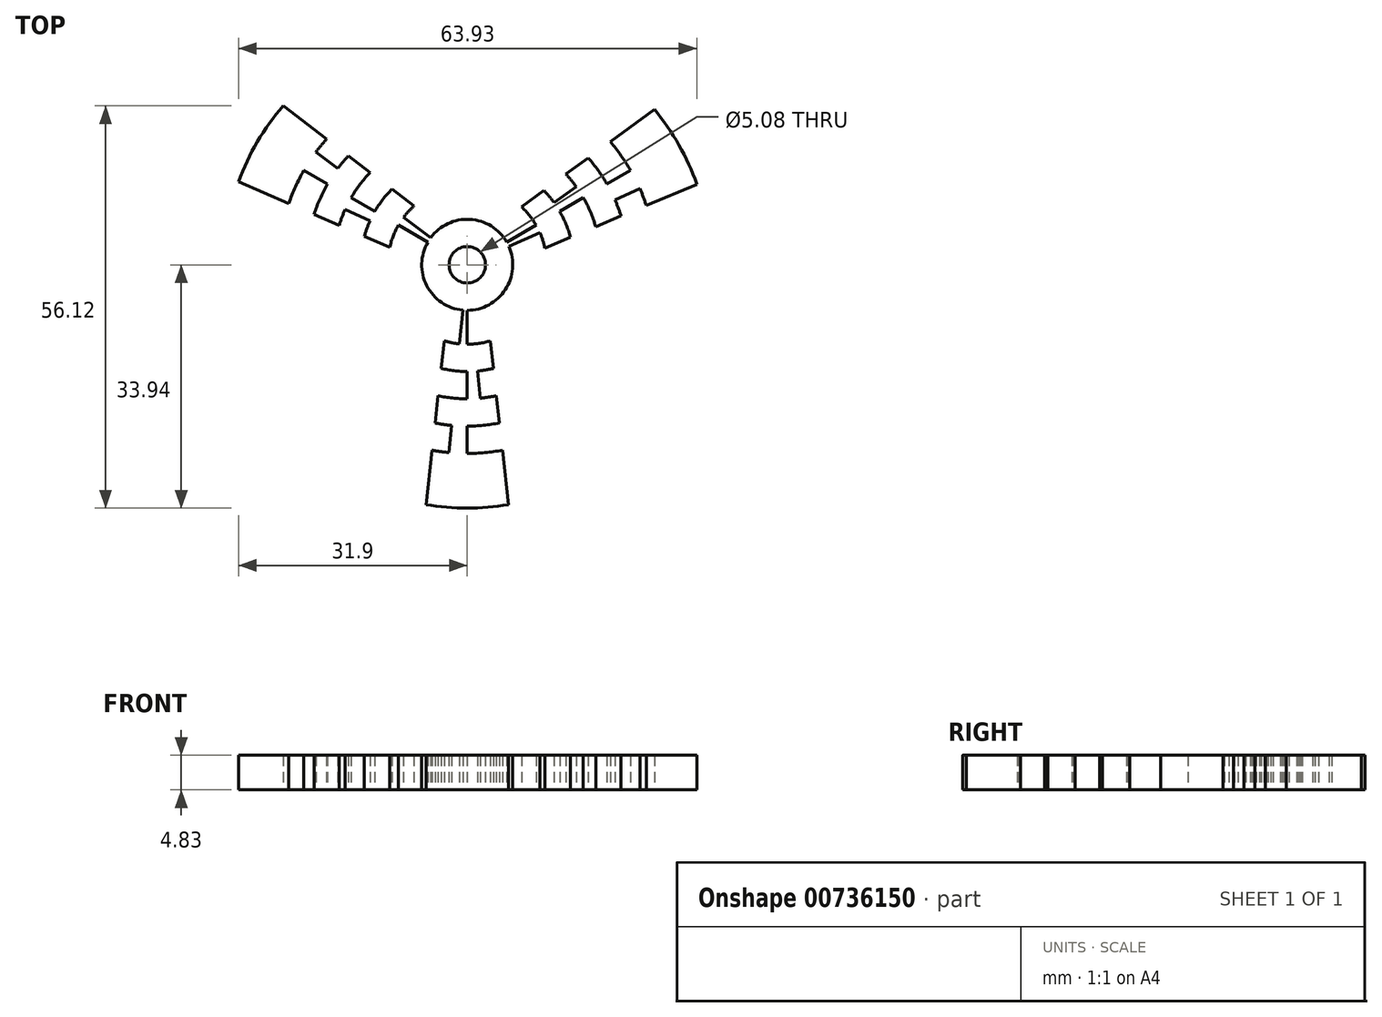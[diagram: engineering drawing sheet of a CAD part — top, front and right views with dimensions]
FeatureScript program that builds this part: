
annotation { "Feature Type Name" : "Feature", "Feature Type Description" : "" }
export const myFeature = defineFeature(function(context is Context, id is Id, definition is map)
    precondition{}
    {
        {
            var Q0;
            Q0=qCreatedBy(makeId("Top.planeOp"),FACE);
            var sketch = newSketch(context, id + "F0", { "sketchPlane" : qUnion([Q0])});
            skCircle(sketch, "E0", {"center": v(0, 0) * mm, "radius": 6.35 * mm});
            skCircle(sketch, "E1", {"center": v(0, 0) * mm, "radius": 11.08 * mm});
            skCircle(sketch, "E2", {"center": v(0, 0) * mm, "radius": 39.37 * mm});
            skCircle(sketch, "E3", {"center": v(0, 0) * mm, "radius": 33.94 * mm});
            skCircle(sketch, "E4", {"center": v(0, 0) * mm, "radius": 26.32 * mm});
            skCircle(sketch, "E5", {"center": v(0, 0) * mm, "radius": 22.51 * mm});
            skCircle(sketch, "E6", {"center": v(0, 0) * mm, "radius": 30.13 * mm});
            skCircle(sketch, "E7", {"center": v(0, 0) * mm, "radius": 14.9 * mm});
            skCircle(sketch, "E8", {"center": v(0, 0) * mm, "radius": 18.7 * mm});
            skCircle(sketch, "E9", {"center": v(0, 0) * mm, "radius": 2.54 * mm});
            skCircle(sketch, "E10", {"center": v(0, 0) * mm, "radius": 37.75 * mm});
            skCircle(sketch, "E11", {"center": v(0, 0) * mm, "radius": 41.56 * mm});
            skCircle(sketch, "E12.cCircle", {"center": v(0, 0) * mm, "radius": 2.54 * mm, "construction": true});
            skLineSegment(sketch, "E12.0", {"start": v(0, -2.54) * mm, "end": v(-2.2, 1.27) * mm});
            skLineSegment(sketch, "E12.1", {"start": v(-2.2, 1.27) * mm, "end": v(2.2, 1.27) * mm});
            skLineSegment(sketch, "E12.2", {"start": v(2.2, 1.27) * mm, "end": v(0, -2.54) * mm});
            skLineSegment(sketch, "E13", {"start": v(0, -39.37) * mm, "end": v(0, 0) * mm});
            skLineSegment(sketch, "E14", {"start": v(34.1, 19.68) * mm, "end": v(0, 0) * mm});
            skLineSegment(sketch, "E15", {"start": v(-34.1, 19.69) * mm, "end": v(0, 0) * mm});
            skLineSegment(sketch, "E16", {"start": v(32.03, 22.89) * mm, "end": v(0, 0) * mm});
            skLineSegment(sketch, "E17", {"start": v(30.5, 24.9) * mm, "end": v(0, 2.54) * mm});
            skLineSegment(sketch, "E18", {"start": v(36.03, 15.87) * mm, "end": v(0, 0) * mm});
            skLineSegment(sketch, "E19", {"start": v(37.04, 13.33) * mm, "end": v(2.2, -1.27) * mm});
            skLineSegment(sketch, "E20", {"start": v(2.2, -1.27) * mm, "end": v(6.33, -38.86) * mm});
            skLineSegment(sketch, "E21", {"start": v(3.81, -39.19) * mm, "end": v(0, 0) * mm});
            skLineSegment(sketch, "E22", {"start": v(-3.81, -39.19) * mm, "end": v(0, 0) * mm});
            skLineSegment(sketch, "E23", {"start": v(-6.33, -38.86) * mm, "end": v(-2.2, -1.27) * mm});
            skLineSegment(sketch, "E24", {"start": v(-2.2, -1.27) * mm, "end": v(-36.89, 13.76) * mm});
            skLineSegment(sketch, "E25", {"start": v(-35.84, 16.3) * mm, "end": v(0, 0) * mm});
            skLineSegment(sketch, "E26", {"start": v(-31.6, 23.5) * mm, "end": v(0, 0) * mm});
            skLineSegment(sketch, "E27", {"start": v(-30.01, 25.48) * mm, "end": v(0, 2.54) * mm});
            skLineSegment(sketch, "E28.0", {"start": v(0, 2.54) * mm, "end": v(2.2, -1.27) * mm});
            skLineSegment(sketch, "E28.1", {"start": v(2.2, -1.27) * mm, "end": v(-2.2, -1.27) * mm});
            skLineSegment(sketch, "E28.2", {"start": v(-2.2, -1.27) * mm, "end": v(0, 2.54) * mm});
            skSolve(sketch);
        }
        {
            var Q0;
            {var subQ0=sQuery(id+"F0.wireOp",EDGE,"E15");var subQ1=sQuery(id+"F0.wireOp",EDGE,"E4");var subQ2=makeQuery(id+"F0.imprint","INTERSECT",VERTEX,{"derivedFrom":[subQ1,subQ0]});Q0=makeQuery(id+"F0.imprint","IMPRINT",FACE,{"disambiguationData":[TD([[makeQuery(id+"F0.imprint","IMPRINT",EDGE,{"disambiguationData":[TD([[subQ2,-1.0]])],"derivedFrom":subQ1}),-1.0]])]});}
            var Q1;
            {var subQ0=sQuery(id+"F0.wireOp",EDGE,"E25");var subQ1=sQuery(id+"F0.wireOp",EDGE,"E0");var subQ2=makeQuery(id+"F0.imprint","INTERSECT",VERTEX,{"derivedFrom":[subQ1,subQ0]});Q1=makeQuery(id+"F0.imprint","IMPRINT",FACE,{"disambiguationData":[TD([[makeQuery(id+"F0.imprint","IMPRINT",EDGE,{"disambiguationData":[TD([[subQ2,-1.0]])],"derivedFrom":subQ1}),1.0]])]});}
            var Q2;
            {var subQ0=sQuery(id+"F0.wireOp",EDGE,"E15");var subQ1=sQuery(id+"F0.wireOp",EDGE,"E0");var subQ2=makeQuery(id+"F0.imprint","INTERSECT",VERTEX,{"derivedFrom":[subQ1,subQ0]});Q2=makeQuery(id+"F0.imprint","IMPRINT",FACE,{"disambiguationData":[TD([[makeQuery(id+"F0.imprint","IMPRINT",EDGE,{"disambiguationData":[TD([[subQ2,-1.0]])],"derivedFrom":subQ1}),1.0]])]});}
            var Q3;
            {var subQ0=sQuery(id+"F0.wireOp",EDGE,"E26");var subQ1=sQuery(id+"F0.wireOp",EDGE,"E0");var subQ2=makeQuery(id+"F0.imprint","INTERSECT",VERTEX,{"derivedFrom":[subQ1,subQ0]});Q3=makeQuery(id+"F0.imprint","IMPRINT",FACE,{"disambiguationData":[TD([[makeQuery(id+"F0.imprint","IMPRINT",EDGE,{"disambiguationData":[TD([[subQ2,-1.0]])],"derivedFrom":subQ1}),1.0]])]});}
            var Q4;
            {var subQ0=sQuery(id+"F0.wireOp",EDGE,"E27");var subQ1=sQuery(id+"F0.wireOp",EDGE,"E0");var subQ2=makeQuery(id+"F0.imprint","INTERSECT",VERTEX,{"derivedFrom":[subQ1,subQ0]});Q4=makeQuery(id+"F0.imprint","IMPRINT",FACE,{"disambiguationData":[TD([[makeQuery(id+"F0.imprint","IMPRINT",EDGE,{"disambiguationData":[TD([[subQ2,-1.0]])],"derivedFrom":subQ1}),1.0]])]});}
            var Q5;
            {var subQ0=sQuery(id+"F0.wireOp",EDGE,"E17");var subQ1=sQuery(id+"F0.wireOp",EDGE,"E0");var subQ2=makeQuery(id+"F0.imprint","INTERSECT",VERTEX,{"derivedFrom":[subQ1,subQ0]});Q5=makeQuery(id+"F0.imprint","IMPRINT",FACE,{"disambiguationData":[TD([[makeQuery(id+"F0.imprint","IMPRINT",EDGE,{"disambiguationData":[TD([[subQ2,-1.0]])],"derivedFrom":subQ1}),1.0]])]});}
            var Q6;
            {var subQ0=sQuery(id+"F0.wireOp",EDGE,"E16");var subQ1=sQuery(id+"F0.wireOp",EDGE,"E0");var subQ2=makeQuery(id+"F0.imprint","INTERSECT",VERTEX,{"derivedFrom":[subQ1,subQ0]});Q6=makeQuery(id+"F0.imprint","IMPRINT",FACE,{"disambiguationData":[TD([[makeQuery(id+"F0.imprint","IMPRINT",EDGE,{"disambiguationData":[TD([[subQ2,-1.0]])],"derivedFrom":subQ1}),1.0]])]});}
            var Q7;
            {var subQ0=sQuery(id+"F0.wireOp",EDGE,"E14");var subQ1=sQuery(id+"F0.wireOp",EDGE,"E0");var subQ2=makeQuery(id+"F0.imprint","INTERSECT",VERTEX,{"derivedFrom":[subQ1,subQ0]});Q7=makeQuery(id+"F0.imprint","IMPRINT",FACE,{"disambiguationData":[TD([[makeQuery(id+"F0.imprint","IMPRINT",EDGE,{"disambiguationData":[TD([[subQ2,-1.0]])],"derivedFrom":subQ1}),1.0]])]});}
            var Q8;
            {var subQ0=sQuery(id+"F0.wireOp",EDGE,"E18");var subQ1=sQuery(id+"F0.wireOp",EDGE,"E0");var subQ2=makeQuery(id+"F0.imprint","INTERSECT",VERTEX,{"derivedFrom":[subQ1,subQ0]});Q8=makeQuery(id+"F0.imprint","IMPRINT",FACE,{"disambiguationData":[TD([[makeQuery(id+"F0.imprint","IMPRINT",EDGE,{"disambiguationData":[TD([[subQ2,-1.0]])],"derivedFrom":subQ1}),1.0]])]});}
            var Q9;
            {var subQ0=sQuery(id+"F0.wireOp",EDGE,"E18");var subQ1=sQuery(id+"F0.wireOp",EDGE,"E0");var subQ2=makeQuery(id+"F0.imprint","INTERSECT",VERTEX,{"derivedFrom":[subQ1,subQ0]});Q9=makeQuery(id+"F0.imprint","IMPRINT",FACE,{"disambiguationData":[TD([[makeQuery(id+"F0.imprint","IMPRINT",EDGE,{"disambiguationData":[TD([[subQ2,1.0]])],"derivedFrom":subQ1}),1.0]])]});}
            var Q10;
            {var subQ0=sQuery(id+"F0.wireOp",EDGE,"E19");var subQ1=sQuery(id+"F0.wireOp",EDGE,"E0");var subQ2=makeQuery(id+"F0.imprint","INTERSECT",VERTEX,{"derivedFrom":[subQ1,subQ0]});Q10=makeQuery(id+"F0.imprint","IMPRINT",FACE,{"disambiguationData":[TD([[makeQuery(id+"F0.imprint","IMPRINT",EDGE,{"disambiguationData":[TD([[subQ2,1.0]])],"derivedFrom":subQ1}),1.0]])]});}
            var Q11;
            {var subQ0=sQuery(id+"F0.wireOp",EDGE,"E21");var subQ1=sQuery(id+"F0.wireOp",EDGE,"E0");var subQ2=makeQuery(id+"F0.imprint","INTERSECT",VERTEX,{"derivedFrom":[subQ1,subQ0]});Q11=makeQuery(id+"F0.imprint","IMPRINT",FACE,{"disambiguationData":[TD([[makeQuery(id+"F0.imprint","IMPRINT",EDGE,{"disambiguationData":[TD([[subQ2,-1.0]])],"derivedFrom":subQ1}),1.0]])]});}
            var Q12;
            {var subQ0=sQuery(id+"F0.wireOp",EDGE,"E13");var subQ1=sQuery(id+"F0.wireOp",EDGE,"E0");var subQ2=makeQuery(id+"F0.imprint","INTERSECT",VERTEX,{"derivedFrom":[subQ1,subQ0]});Q12=makeQuery(id+"F0.imprint","IMPRINT",FACE,{"disambiguationData":[TD([[makeQuery(id+"F0.imprint","IMPRINT",EDGE,{"disambiguationData":[TD([[subQ2,-1.0]])],"derivedFrom":subQ1}),1.0]])]});}
            var Q13;
            {var subQ0=sQuery(id+"F0.wireOp",EDGE,"E22");var subQ1=sQuery(id+"F0.wireOp",EDGE,"E0");var subQ2=makeQuery(id+"F0.imprint","INTERSECT",VERTEX,{"derivedFrom":[subQ1,subQ0]});Q13=makeQuery(id+"F0.imprint","IMPRINT",FACE,{"disambiguationData":[TD([[makeQuery(id+"F0.imprint","IMPRINT",EDGE,{"disambiguationData":[TD([[subQ2,-1.0]])],"derivedFrom":subQ1}),1.0]])]});}
            var Q14;
            {var subQ0=sQuery(id+"F0.wireOp",EDGE,"E23");var subQ1=sQuery(id+"F0.wireOp",EDGE,"E0");var subQ2=makeQuery(id+"F0.imprint","INTERSECT",VERTEX,{"derivedFrom":[subQ1,subQ0]});Q14=makeQuery(id+"F0.imprint","IMPRINT",FACE,{"disambiguationData":[TD([[makeQuery(id+"F0.imprint","IMPRINT",EDGE,{"disambiguationData":[TD([[subQ2,-1.0]])],"derivedFrom":subQ1}),1.0]])]});}
            var Q15;
            {var subQ0=sQuery(id+"F0.wireOp",EDGE,"E24");var subQ1=sQuery(id+"F0.wireOp",EDGE,"E0");var subQ2=makeQuery(id+"F0.imprint","INTERSECT",VERTEX,{"derivedFrom":[subQ1,subQ0]});Q15=makeQuery(id+"F0.imprint","IMPRINT",FACE,{"disambiguationData":[TD([[makeQuery(id+"F0.imprint","IMPRINT",EDGE,{"disambiguationData":[TD([[subQ2,-1.0]])],"derivedFrom":subQ1}),1.0]])]});}
            var Q16;
            {var subQ0=sQuery(id+"F0.wireOp",EDGE,"E27");var subQ1=sQuery(id+"F0.wireOp",EDGE,"E4");var subQ2=makeQuery(id+"F0.imprint","INTERSECT",VERTEX,{"derivedFrom":[subQ1,subQ0]});Q16=makeQuery(id+"F0.imprint","IMPRINT",FACE,{"disambiguationData":[TD([[makeQuery(id+"F0.imprint","IMPRINT",EDGE,{"disambiguationData":[TD([[subQ2,-1.0]])],"derivedFrom":subQ1}),-1.0]])]});}
            var Q17;
            {var subQ0=sQuery(id+"F0.wireOp",EDGE,"E26");var subQ1=sQuery(id+"F0.wireOp",EDGE,"E4");var subQ2=makeQuery(id+"F0.imprint","INTERSECT",VERTEX,{"derivedFrom":[subQ1,subQ0]});Q17=makeQuery(id+"F0.imprint","IMPRINT",FACE,{"disambiguationData":[TD([[makeQuery(id+"F0.imprint","IMPRINT",EDGE,{"disambiguationData":[TD([[subQ2,-1.0]])],"derivedFrom":subQ1}),-1.0]])]});}
            var Q18;
            {var subQ0=sQuery(id+"F0.wireOp",EDGE,"E25");var subQ1=sQuery(id+"F0.wireOp",EDGE,"E4");var subQ2=makeQuery(id+"F0.imprint","INTERSECT",VERTEX,{"derivedFrom":[subQ1,subQ0]});Q18=makeQuery(id+"F0.imprint","IMPRINT",FACE,{"disambiguationData":[TD([[makeQuery(id+"F0.imprint","IMPRINT",EDGE,{"disambiguationData":[TD([[subQ2,-1.0]])],"derivedFrom":subQ1}),-1.0]])]});}
            var Q19;
            {var subQ0=sQuery(id+"F0.wireOp",EDGE,"E25");var subQ1=sQuery(id+"F0.wireOp",EDGE,"E5");var subQ2=makeQuery(id+"F0.imprint","INTERSECT",VERTEX,{"derivedFrom":[subQ1,subQ0]});Q19=makeQuery(id+"F0.imprint","IMPRINT",FACE,{"disambiguationData":[TD([[makeQuery(id+"F0.imprint","IMPRINT",EDGE,{"disambiguationData":[TD([[subQ2,-1.0]])],"derivedFrom":subQ1}),1.0]])]});}
            var Q20;
            {var subQ0=sQuery(id+"F0.wireOp",EDGE,"E15");var subQ1=sQuery(id+"F0.wireOp",EDGE,"E5");var subQ2=makeQuery(id+"F0.imprint","INTERSECT",VERTEX,{"derivedFrom":[subQ1,subQ0]});Q20=makeQuery(id+"F0.imprint","IMPRINT",FACE,{"disambiguationData":[TD([[makeQuery(id+"F0.imprint","IMPRINT",EDGE,{"disambiguationData":[TD([[subQ2,-1.0]])],"derivedFrom":subQ1}),1.0]])]});}
            var Q21;
            {var subQ0=sQuery(id+"F0.wireOp",EDGE,"E26");var subQ1=sQuery(id+"F0.wireOp",EDGE,"E5");var subQ2=makeQuery(id+"F0.imprint","INTERSECT",VERTEX,{"derivedFrom":[subQ1,subQ0]});Q21=makeQuery(id+"F0.imprint","IMPRINT",FACE,{"disambiguationData":[TD([[makeQuery(id+"F0.imprint","IMPRINT",EDGE,{"disambiguationData":[TD([[subQ2,-1.0]])],"derivedFrom":subQ1}),1.0]])]});}
            var Q22;
            {var subQ0=sQuery(id+"F0.wireOp",EDGE,"E27");var subQ1=sQuery(id+"F0.wireOp",EDGE,"E5");var subQ2=makeQuery(id+"F0.imprint","INTERSECT",VERTEX,{"derivedFrom":[subQ1,subQ0]});Q22=makeQuery(id+"F0.imprint","IMPRINT",FACE,{"disambiguationData":[TD([[makeQuery(id+"F0.imprint","IMPRINT",EDGE,{"disambiguationData":[TD([[subQ2,-1.0]])],"derivedFrom":subQ1}),1.0]])]});}
            var Q23;
            {var subQ0=sQuery(id+"F0.wireOp",EDGE,"E27");var subQ1=sQuery(id+"F0.wireOp",EDGE,"E1");var subQ2=makeQuery(id+"F0.imprint","INTERSECT",VERTEX,{"derivedFrom":[subQ1,subQ0]});Q23=makeQuery(id+"F0.imprint","IMPRINT",FACE,{"disambiguationData":[TD([[makeQuery(id+"F0.imprint","IMPRINT",EDGE,{"disambiguationData":[TD([[subQ2,-1.0]])],"derivedFrom":subQ1}),-1.0]])]});}
            var Q24;
            {var subQ0=sQuery(id+"F0.wireOp",EDGE,"E26");var subQ1=sQuery(id+"F0.wireOp",EDGE,"E1");var subQ2=makeQuery(id+"F0.imprint","INTERSECT",VERTEX,{"derivedFrom":[subQ1,subQ0]});Q24=makeQuery(id+"F0.imprint","IMPRINT",FACE,{"disambiguationData":[TD([[makeQuery(id+"F0.imprint","IMPRINT",EDGE,{"disambiguationData":[TD([[subQ2,-1.0]])],"derivedFrom":subQ1}),-1.0]])]});}
            var Q25;
            {var subQ0=sQuery(id+"F0.wireOp",EDGE,"E15");var subQ1=sQuery(id+"F0.wireOp",EDGE,"E1");var subQ2=makeQuery(id+"F0.imprint","INTERSECT",VERTEX,{"derivedFrom":[subQ1,subQ0]});Q25=makeQuery(id+"F0.imprint","IMPRINT",FACE,{"disambiguationData":[TD([[makeQuery(id+"F0.imprint","IMPRINT",EDGE,{"disambiguationData":[TD([[subQ2,-1.0]])],"derivedFrom":subQ1}),-1.0]])]});}
            var Q26;
            {var subQ0=sQuery(id+"F0.wireOp",EDGE,"E25");var subQ1=sQuery(id+"F0.wireOp",EDGE,"E1");var subQ2=makeQuery(id+"F0.imprint","INTERSECT",VERTEX,{"derivedFrom":[subQ1,subQ0]});Q26=makeQuery(id+"F0.imprint","IMPRINT",FACE,{"disambiguationData":[TD([[makeQuery(id+"F0.imprint","IMPRINT",EDGE,{"disambiguationData":[TD([[subQ2,-1.0]])],"derivedFrom":subQ1}),-1.0]])]});}
            var Q27;
            {var subQ0=sQuery(id+"F0.wireOp",EDGE,"E26");var subQ1=sQuery(id+"F0.wireOp",EDGE,"E0");var subQ2=makeQuery(id+"F0.imprint","INTERSECT",VERTEX,{"derivedFrom":[subQ1,subQ0]});Q27=makeQuery(id+"F0.imprint","IMPRINT",FACE,{"disambiguationData":[TD([[makeQuery(id+"F0.imprint","IMPRINT",EDGE,{"disambiguationData":[TD([[subQ2,-1.0]])],"derivedFrom":subQ1}),-1.0]])]});}
            var Q28;
            {var subQ0=sQuery(id+"F0.wireOp",EDGE,"E15");var subQ1=sQuery(id+"F0.wireOp",EDGE,"E7");var subQ2=makeQuery(id+"F0.imprint","INTERSECT",VERTEX,{"derivedFrom":[subQ1,subQ0]});Q28=makeQuery(id+"F0.imprint","IMPRINT",FACE,{"disambiguationData":[TD([[makeQuery(id+"F0.imprint","IMPRINT",EDGE,{"disambiguationData":[TD([[subQ2,-1.0]])],"derivedFrom":subQ1}),-1.0]])]});}
            var Q29;
            {var subQ0=sQuery(id+"F0.wireOp",EDGE,"E26");var subQ1=sQuery(id+"F0.wireOp",EDGE,"E4");var subQ2=makeQuery(id+"F0.imprint","INTERSECT",VERTEX,{"derivedFrom":[subQ1,subQ0]});Q29=makeQuery(id+"F0.imprint","IMPRINT",FACE,{"disambiguationData":[TD([[makeQuery(id+"F0.imprint","IMPRINT",EDGE,{"disambiguationData":[TD([[subQ2,-1.0]])],"derivedFrom":subQ1}),1.0]])]});}
            var Q30;
            {var subQ0=sQuery(id+"F0.wireOp",EDGE,"E15");var subQ1=sQuery(id+"F0.wireOp",EDGE,"E3");var subQ2=makeQuery(id+"F0.imprint","INTERSECT",VERTEX,{"derivedFrom":[subQ1,subQ0]});Q30=makeQuery(id+"F0.imprint","IMPRINT",FACE,{"disambiguationData":[TD([[makeQuery(id+"F0.imprint","IMPRINT",EDGE,{"disambiguationData":[TD([[subQ2,-1.0]])],"derivedFrom":subQ1}),1.0]])]});}
            var Q31;
            {var subQ0=sQuery(id+"F0.wireOp",EDGE,"E18");var subQ1=sQuery(id+"F0.wireOp",EDGE,"E0");var subQ2=makeQuery(id+"F0.imprint","INTERSECT",VERTEX,{"derivedFrom":[subQ1,subQ0]});Q31=makeQuery(id+"F0.imprint","IMPRINT",FACE,{"disambiguationData":[TD([[makeQuery(id+"F0.imprint","IMPRINT",EDGE,{"disambiguationData":[TD([[subQ2,-1.0]])],"derivedFrom":subQ1}),-1.0]])]});}
            var Q32;
            {var subQ0=sQuery(id+"F0.wireOp",EDGE,"E16");var subQ1=sQuery(id+"F0.wireOp",EDGE,"E1");var subQ2=makeQuery(id+"F0.imprint","INTERSECT",VERTEX,{"derivedFrom":[subQ1,subQ0]});Q32=makeQuery(id+"F0.imprint","IMPRINT",FACE,{"disambiguationData":[TD([[makeQuery(id+"F0.imprint","IMPRINT",EDGE,{"disambiguationData":[TD([[subQ2,-1.0]])],"derivedFrom":subQ1}),-1.0]])]});}
            var Q33;
            {var subQ0=sQuery(id+"F0.wireOp",EDGE,"E14");var subQ1=sQuery(id+"F0.wireOp",EDGE,"E1");var subQ2=makeQuery(id+"F0.imprint","INTERSECT",VERTEX,{"derivedFrom":[subQ1,subQ0]});Q33=makeQuery(id+"F0.imprint","IMPRINT",FACE,{"disambiguationData":[TD([[makeQuery(id+"F0.imprint","IMPRINT",EDGE,{"disambiguationData":[TD([[subQ2,-1.0]])],"derivedFrom":subQ1}),-1.0]])]});}
            var Q34;
            {var subQ0=sQuery(id+"F0.wireOp",EDGE,"E18");var subQ1=sQuery(id+"F0.wireOp",EDGE,"E1");var subQ2=makeQuery(id+"F0.imprint","INTERSECT",VERTEX,{"derivedFrom":[subQ1,subQ0]});Q34=makeQuery(id+"F0.imprint","IMPRINT",FACE,{"disambiguationData":[TD([[makeQuery(id+"F0.imprint","IMPRINT",EDGE,{"disambiguationData":[TD([[subQ2,-1.0]])],"derivedFrom":subQ1}),-1.0]])]});}
            var Q35;
            {var subQ0=sQuery(id+"F0.wireOp",EDGE,"E18");var subQ1=sQuery(id+"F0.wireOp",EDGE,"E1");var subQ2=makeQuery(id+"F0.imprint","INTERSECT",VERTEX,{"derivedFrom":[subQ1,subQ0]});Q35=makeQuery(id+"F0.imprint","IMPRINT",FACE,{"disambiguationData":[TD([[makeQuery(id+"F0.imprint","IMPRINT",EDGE,{"disambiguationData":[TD([[subQ2,1.0]])],"derivedFrom":subQ1}),-1.0]])]});}
            var Q36;
            {var subQ0=sQuery(id+"F0.wireOp",EDGE,"E16");var subQ1=sQuery(id+"F0.wireOp",EDGE,"E5");var subQ2=makeQuery(id+"F0.imprint","INTERSECT",VERTEX,{"derivedFrom":[subQ1,subQ0]});Q36=makeQuery(id+"F0.imprint","IMPRINT",FACE,{"disambiguationData":[TD([[makeQuery(id+"F0.imprint","IMPRINT",EDGE,{"disambiguationData":[TD([[subQ2,-1.0]])],"derivedFrom":subQ1}),1.0]])]});}
            var Q37;
            {var subQ0=sQuery(id+"F0.wireOp",EDGE,"E14");var subQ1=sQuery(id+"F0.wireOp",EDGE,"E5");var subQ2=makeQuery(id+"F0.imprint","INTERSECT",VERTEX,{"derivedFrom":[subQ1,subQ0]});Q37=makeQuery(id+"F0.imprint","IMPRINT",FACE,{"disambiguationData":[TD([[makeQuery(id+"F0.imprint","IMPRINT",EDGE,{"disambiguationData":[TD([[subQ2,-1.0]])],"derivedFrom":subQ1}),1.0]])]});}
            var Q38;
            {var subQ0=sQuery(id+"F0.wireOp",EDGE,"E18");var subQ1=sQuery(id+"F0.wireOp",EDGE,"E5");var subQ2=makeQuery(id+"F0.imprint","INTERSECT",VERTEX,{"derivedFrom":[subQ1,subQ0]});Q38=makeQuery(id+"F0.imprint","IMPRINT",FACE,{"disambiguationData":[TD([[makeQuery(id+"F0.imprint","IMPRINT",EDGE,{"disambiguationData":[TD([[subQ2,-1.0]])],"derivedFrom":subQ1}),1.0]])]});}
            var Q39;
            {var subQ0=sQuery(id+"F0.wireOp",EDGE,"E18");var subQ1=sQuery(id+"F0.wireOp",EDGE,"E5");var subQ2=makeQuery(id+"F0.imprint","INTERSECT",VERTEX,{"derivedFrom":[subQ1,subQ0]});Q39=makeQuery(id+"F0.imprint","IMPRINT",FACE,{"disambiguationData":[TD([[makeQuery(id+"F0.imprint","IMPRINT",EDGE,{"disambiguationData":[TD([[subQ2,1.0]])],"derivedFrom":subQ1}),1.0]])]});}
            var Q40;
            {var subQ0=sQuery(id+"F0.wireOp",EDGE,"E14");var subQ1=sQuery(id+"F0.wireOp",EDGE,"E7");var subQ2=makeQuery(id+"F0.imprint","INTERSECT",VERTEX,{"derivedFrom":[subQ1,subQ0]});Q40=makeQuery(id+"F0.imprint","IMPRINT",FACE,{"disambiguationData":[TD([[makeQuery(id+"F0.imprint","IMPRINT",EDGE,{"disambiguationData":[TD([[subQ2,-1.0]])],"derivedFrom":subQ1}),-1.0]])]});}
            var Q41;
            {var subQ0=sQuery(id+"F0.wireOp",EDGE,"E18");var subQ1=sQuery(id+"F0.wireOp",EDGE,"E4");var subQ2=makeQuery(id+"F0.imprint","INTERSECT",VERTEX,{"derivedFrom":[subQ1,subQ0]});Q41=makeQuery(id+"F0.imprint","IMPRINT",FACE,{"disambiguationData":[TD([[makeQuery(id+"F0.imprint","IMPRINT",EDGE,{"disambiguationData":[TD([[subQ2,-1.0]])],"derivedFrom":subQ1}),1.0]])]});}
            var Q42;
            {var subQ0=sQuery(id+"F0.wireOp",EDGE,"E16");var subQ1=sQuery(id+"F0.wireOp",EDGE,"E4");var subQ2=makeQuery(id+"F0.imprint","INTERSECT",VERTEX,{"derivedFrom":[subQ1,subQ0]});Q42=makeQuery(id+"F0.imprint","IMPRINT",FACE,{"disambiguationData":[TD([[makeQuery(id+"F0.imprint","IMPRINT",EDGE,{"disambiguationData":[TD([[subQ2,-1.0]])],"derivedFrom":subQ1}),-1.0]])]});}
            var Q43;
            {var subQ0=sQuery(id+"F0.wireOp",EDGE,"E14");var subQ1=sQuery(id+"F0.wireOp",EDGE,"E4");var subQ2=makeQuery(id+"F0.imprint","INTERSECT",VERTEX,{"derivedFrom":[subQ1,subQ0]});Q43=makeQuery(id+"F0.imprint","IMPRINT",FACE,{"disambiguationData":[TD([[makeQuery(id+"F0.imprint","IMPRINT",EDGE,{"disambiguationData":[TD([[subQ2,-1.0]])],"derivedFrom":subQ1}),-1.0]])]});}
            var Q44;
            {var subQ0=sQuery(id+"F0.wireOp",EDGE,"E18");var subQ1=sQuery(id+"F0.wireOp",EDGE,"E4");var subQ2=makeQuery(id+"F0.imprint","INTERSECT",VERTEX,{"derivedFrom":[subQ1,subQ0]});Q44=makeQuery(id+"F0.imprint","IMPRINT",FACE,{"disambiguationData":[TD([[makeQuery(id+"F0.imprint","IMPRINT",EDGE,{"disambiguationData":[TD([[subQ2,-1.0]])],"derivedFrom":subQ1}),-1.0]])]});}
            var Q45;
            {var subQ0=sQuery(id+"F0.wireOp",EDGE,"E18");var subQ1=sQuery(id+"F0.wireOp",EDGE,"E4");var subQ2=makeQuery(id+"F0.imprint","INTERSECT",VERTEX,{"derivedFrom":[subQ1,subQ0]});Q45=makeQuery(id+"F0.imprint","IMPRINT",FACE,{"disambiguationData":[TD([[makeQuery(id+"F0.imprint","IMPRINT",EDGE,{"disambiguationData":[TD([[subQ2,1.0]])],"derivedFrom":subQ1}),-1.0]])]});}
            var Q46;
            {var subQ0=sQuery(id+"F0.wireOp",EDGE,"E16");var subQ1=sQuery(id+"F0.wireOp",EDGE,"E3");var subQ2=makeQuery(id+"F0.imprint","INTERSECT",VERTEX,{"derivedFrom":[subQ1,subQ0]});Q46=makeQuery(id+"F0.imprint","IMPRINT",FACE,{"disambiguationData":[TD([[makeQuery(id+"F0.imprint","IMPRINT",EDGE,{"disambiguationData":[TD([[subQ2,-1.0]])],"derivedFrom":subQ1}),1.0]])]});}
            var Q47;
            {var subQ0=sQuery(id+"F0.wireOp",EDGE,"E14");var subQ1=sQuery(id+"F0.wireOp",EDGE,"E3");var subQ2=makeQuery(id+"F0.imprint","INTERSECT",VERTEX,{"derivedFrom":[subQ1,subQ0]});Q47=makeQuery(id+"F0.imprint","IMPRINT",FACE,{"disambiguationData":[TD([[makeQuery(id+"F0.imprint","IMPRINT",EDGE,{"disambiguationData":[TD([[subQ2,-1.0]])],"derivedFrom":subQ1}),1.0]])]});}
            var Q48;
            {var subQ0=sQuery(id+"F0.wireOp",EDGE,"E18");var subQ1=sQuery(id+"F0.wireOp",EDGE,"E3");var subQ2=makeQuery(id+"F0.imprint","INTERSECT",VERTEX,{"derivedFrom":[subQ1,subQ0]});Q48=makeQuery(id+"F0.imprint","IMPRINT",FACE,{"disambiguationData":[TD([[makeQuery(id+"F0.imprint","IMPRINT",EDGE,{"disambiguationData":[TD([[subQ2,-1.0]])],"derivedFrom":subQ1}),1.0]])]});}
            var Q49;
            {var subQ0=sQuery(id+"F0.wireOp",EDGE,"E18");var subQ1=sQuery(id+"F0.wireOp",EDGE,"E3");var subQ2=makeQuery(id+"F0.imprint","INTERSECT",VERTEX,{"derivedFrom":[subQ1,subQ0]});Q49=makeQuery(id+"F0.imprint","IMPRINT",FACE,{"disambiguationData":[TD([[makeQuery(id+"F0.imprint","IMPRINT",EDGE,{"disambiguationData":[TD([[subQ2,1.0]])],"derivedFrom":subQ1}),1.0]])]});}
            var Q50;
            {var subQ0=sQuery(id+"F0.wireOp",EDGE,"E25");var subQ1=sQuery(id+"F0.wireOp",EDGE,"E3");var subQ2=makeQuery(id+"F0.imprint","INTERSECT",VERTEX,{"derivedFrom":[subQ1,subQ0]});Q50=makeQuery(id+"F0.imprint","IMPRINT",FACE,{"disambiguationData":[TD([[makeQuery(id+"F0.imprint","IMPRINT",EDGE,{"disambiguationData":[TD([[subQ2,-1.0]])],"derivedFrom":subQ1}),1.0]])]});}
            var Q51;
            {var subQ0=sQuery(id+"F0.wireOp",EDGE,"E26");var subQ1=sQuery(id+"F0.wireOp",EDGE,"E3");var subQ2=makeQuery(id+"F0.imprint","INTERSECT",VERTEX,{"derivedFrom":[subQ1,subQ0]});Q51=makeQuery(id+"F0.imprint","IMPRINT",FACE,{"disambiguationData":[TD([[makeQuery(id+"F0.imprint","IMPRINT",EDGE,{"disambiguationData":[TD([[subQ2,-1.0]])],"derivedFrom":subQ1}),1.0]])]});}
            var Q52;
            {var subQ0=sQuery(id+"F0.wireOp",EDGE,"E27");var subQ1=sQuery(id+"F0.wireOp",EDGE,"E3");var subQ2=makeQuery(id+"F0.imprint","INTERSECT",VERTEX,{"derivedFrom":[subQ1,subQ0]});Q52=makeQuery(id+"F0.imprint","IMPRINT",FACE,{"disambiguationData":[TD([[makeQuery(id+"F0.imprint","IMPRINT",EDGE,{"disambiguationData":[TD([[subQ2,-1.0]])],"derivedFrom":subQ1}),1.0]])]});}
            var Q53;
            {var subQ0=sQuery(id+"F0.wireOp",EDGE,"E22");var subQ1=sQuery(id+"F0.wireOp",EDGE,"E0");var subQ2=makeQuery(id+"F0.imprint","INTERSECT",VERTEX,{"derivedFrom":[subQ1,subQ0]});Q53=makeQuery(id+"F0.imprint","IMPRINT",FACE,{"disambiguationData":[TD([[makeQuery(id+"F0.imprint","IMPRINT",EDGE,{"disambiguationData":[TD([[subQ2,-1.0]])],"derivedFrom":subQ1}),-1.0]])]});}
            var Q54;
            {var subQ0=sQuery(id+"F0.wireOp",EDGE,"E23");var subQ1=sQuery(id+"F0.wireOp",EDGE,"E1");var subQ2=makeQuery(id+"F0.imprint","INTERSECT",VERTEX,{"derivedFrom":[subQ1,subQ0]});Q54=makeQuery(id+"F0.imprint","IMPRINT",FACE,{"disambiguationData":[TD([[makeQuery(id+"F0.imprint","IMPRINT",EDGE,{"disambiguationData":[TD([[subQ2,-1.0]])],"derivedFrom":subQ1}),-1.0]])]});}
            var Q55;
            {var subQ0=sQuery(id+"F0.wireOp",EDGE,"E22");var subQ1=sQuery(id+"F0.wireOp",EDGE,"E1");var subQ2=makeQuery(id+"F0.imprint","INTERSECT",VERTEX,{"derivedFrom":[subQ1,subQ0]});Q55=makeQuery(id+"F0.imprint","IMPRINT",FACE,{"disambiguationData":[TD([[makeQuery(id+"F0.imprint","IMPRINT",EDGE,{"disambiguationData":[TD([[subQ2,-1.0]])],"derivedFrom":subQ1}),-1.0]])]});}
            var Q56;
            {var subQ0=sQuery(id+"F0.wireOp",EDGE,"E13");var subQ1=sQuery(id+"F0.wireOp",EDGE,"E1");var subQ2=makeQuery(id+"F0.imprint","INTERSECT",VERTEX,{"derivedFrom":[subQ1,subQ0]});Q56=makeQuery(id+"F0.imprint","IMPRINT",FACE,{"disambiguationData":[TD([[makeQuery(id+"F0.imprint","IMPRINT",EDGE,{"disambiguationData":[TD([[subQ2,-1.0]])],"derivedFrom":subQ1}),-1.0]])]});}
            var Q57;
            {var subQ0=sQuery(id+"F0.wireOp",EDGE,"E21");var subQ1=sQuery(id+"F0.wireOp",EDGE,"E1");var subQ2=makeQuery(id+"F0.imprint","INTERSECT",VERTEX,{"derivedFrom":[subQ1,subQ0]});Q57=makeQuery(id+"F0.imprint","IMPRINT",FACE,{"disambiguationData":[TD([[makeQuery(id+"F0.imprint","IMPRINT",EDGE,{"disambiguationData":[TD([[subQ2,-1.0]])],"derivedFrom":subQ1}),-1.0]])]});}
            var Q58;
            {var subQ0=sQuery(id+"F0.wireOp",EDGE,"E13");var subQ1=sQuery(id+"F0.wireOp",EDGE,"E7");var subQ2=makeQuery(id+"F0.imprint","INTERSECT",VERTEX,{"derivedFrom":[subQ1,subQ0]});Q58=makeQuery(id+"F0.imprint","IMPRINT",FACE,{"disambiguationData":[TD([[makeQuery(id+"F0.imprint","IMPRINT",EDGE,{"disambiguationData":[TD([[subQ2,-1.0]])],"derivedFrom":subQ1}),-1.0]])]});}
            var Q59;
            {var subQ0=sQuery(id+"F0.wireOp",EDGE,"E23");var subQ1=sQuery(id+"F0.wireOp",EDGE,"E5");var subQ2=makeQuery(id+"F0.imprint","INTERSECT",VERTEX,{"derivedFrom":[subQ1,subQ0]});Q59=makeQuery(id+"F0.imprint","IMPRINT",FACE,{"disambiguationData":[TD([[makeQuery(id+"F0.imprint","IMPRINT",EDGE,{"disambiguationData":[TD([[subQ2,-1.0]])],"derivedFrom":subQ1}),1.0]])]});}
            var Q60;
            {var subQ0=sQuery(id+"F0.wireOp",EDGE,"E22");var subQ1=sQuery(id+"F0.wireOp",EDGE,"E5");var subQ2=makeQuery(id+"F0.imprint","INTERSECT",VERTEX,{"derivedFrom":[subQ1,subQ0]});Q60=makeQuery(id+"F0.imprint","IMPRINT",FACE,{"disambiguationData":[TD([[makeQuery(id+"F0.imprint","IMPRINT",EDGE,{"disambiguationData":[TD([[subQ2,-1.0]])],"derivedFrom":subQ1}),1.0]])]});}
            var Q61;
            {var subQ0=sQuery(id+"F0.wireOp",EDGE,"E13");var subQ1=sQuery(id+"F0.wireOp",EDGE,"E5");var subQ2=makeQuery(id+"F0.imprint","INTERSECT",VERTEX,{"derivedFrom":[subQ1,subQ0]});Q61=makeQuery(id+"F0.imprint","IMPRINT",FACE,{"disambiguationData":[TD([[makeQuery(id+"F0.imprint","IMPRINT",EDGE,{"disambiguationData":[TD([[subQ2,-1.0]])],"derivedFrom":subQ1}),1.0]])]});}
            var Q62;
            {var subQ0=sQuery(id+"F0.wireOp",EDGE,"E21");var subQ1=sQuery(id+"F0.wireOp",EDGE,"E5");var subQ2=makeQuery(id+"F0.imprint","INTERSECT",VERTEX,{"derivedFrom":[subQ1,subQ0]});Q62=makeQuery(id+"F0.imprint","IMPRINT",FACE,{"disambiguationData":[TD([[makeQuery(id+"F0.imprint","IMPRINT",EDGE,{"disambiguationData":[TD([[subQ2,-1.0]])],"derivedFrom":subQ1}),1.0]])]});}
            var Q63;
            {var subQ0=sQuery(id+"F0.wireOp",EDGE,"E22");var subQ1=sQuery(id+"F0.wireOp",EDGE,"E4");var subQ2=makeQuery(id+"F0.imprint","INTERSECT",VERTEX,{"derivedFrom":[subQ1,subQ0]});Q63=makeQuery(id+"F0.imprint","IMPRINT",FACE,{"disambiguationData":[TD([[makeQuery(id+"F0.imprint","IMPRINT",EDGE,{"disambiguationData":[TD([[subQ2,-1.0]])],"derivedFrom":subQ1}),1.0]])]});}
            var Q64;
            {var subQ0=sQuery(id+"F0.wireOp",EDGE,"E23");var subQ1=sQuery(id+"F0.wireOp",EDGE,"E4");var subQ2=makeQuery(id+"F0.imprint","INTERSECT",VERTEX,{"derivedFrom":[subQ1,subQ0]});Q64=makeQuery(id+"F0.imprint","IMPRINT",FACE,{"disambiguationData":[TD([[makeQuery(id+"F0.imprint","IMPRINT",EDGE,{"disambiguationData":[TD([[subQ2,-1.0]])],"derivedFrom":subQ1}),-1.0]])]});}
            var Q65;
            {var subQ0=sQuery(id+"F0.wireOp",EDGE,"E22");var subQ1=sQuery(id+"F0.wireOp",EDGE,"E4");var subQ2=makeQuery(id+"F0.imprint","INTERSECT",VERTEX,{"derivedFrom":[subQ1,subQ0]});Q65=makeQuery(id+"F0.imprint","IMPRINT",FACE,{"disambiguationData":[TD([[makeQuery(id+"F0.imprint","IMPRINT",EDGE,{"disambiguationData":[TD([[subQ2,-1.0]])],"derivedFrom":subQ1}),-1.0]])]});}
            var Q66;
            {var subQ0=sQuery(id+"F0.wireOp",EDGE,"E13");var subQ1=sQuery(id+"F0.wireOp",EDGE,"E4");var subQ2=makeQuery(id+"F0.imprint","INTERSECT",VERTEX,{"derivedFrom":[subQ1,subQ0]});Q66=makeQuery(id+"F0.imprint","IMPRINT",FACE,{"disambiguationData":[TD([[makeQuery(id+"F0.imprint","IMPRINT",EDGE,{"disambiguationData":[TD([[subQ2,-1.0]])],"derivedFrom":subQ1}),-1.0]])]});}
            var Q67;
            {var subQ0=sQuery(id+"F0.wireOp",EDGE,"E21");var subQ1=sQuery(id+"F0.wireOp",EDGE,"E4");var subQ2=makeQuery(id+"F0.imprint","INTERSECT",VERTEX,{"derivedFrom":[subQ1,subQ0]});Q67=makeQuery(id+"F0.imprint","IMPRINT",FACE,{"disambiguationData":[TD([[makeQuery(id+"F0.imprint","IMPRINT",EDGE,{"disambiguationData":[TD([[subQ2,-1.0]])],"derivedFrom":subQ1}),-1.0]])]});}
            var Q68;
            {var subQ0=sQuery(id+"F0.wireOp",EDGE,"E23");var subQ1=sQuery(id+"F0.wireOp",EDGE,"E3");var subQ2=makeQuery(id+"F0.imprint","INTERSECT",VERTEX,{"derivedFrom":[subQ1,subQ0]});Q68=makeQuery(id+"F0.imprint","IMPRINT",FACE,{"disambiguationData":[TD([[makeQuery(id+"F0.imprint","IMPRINT",EDGE,{"disambiguationData":[TD([[subQ2,-1.0]])],"derivedFrom":subQ1}),1.0]])]});}
            var Q69;
            {var subQ0=sQuery(id+"F0.wireOp",EDGE,"E22");var subQ1=sQuery(id+"F0.wireOp",EDGE,"E3");var subQ2=makeQuery(id+"F0.imprint","INTERSECT",VERTEX,{"derivedFrom":[subQ1,subQ0]});Q69=makeQuery(id+"F0.imprint","IMPRINT",FACE,{"disambiguationData":[TD([[makeQuery(id+"F0.imprint","IMPRINT",EDGE,{"disambiguationData":[TD([[subQ2,-1.0]])],"derivedFrom":subQ1}),1.0]])]});}
            var Q70;
            {var subQ0=sQuery(id+"F0.wireOp",EDGE,"E13");var subQ1=sQuery(id+"F0.wireOp",EDGE,"E3");var subQ2=makeQuery(id+"F0.imprint","INTERSECT",VERTEX,{"derivedFrom":[subQ1,subQ0]});Q70=makeQuery(id+"F0.imprint","IMPRINT",FACE,{"disambiguationData":[TD([[makeQuery(id+"F0.imprint","IMPRINT",EDGE,{"disambiguationData":[TD([[subQ2,-1.0]])],"derivedFrom":subQ1}),1.0]])]});}
            var Q71;
            {var subQ0=sQuery(id+"F0.wireOp",EDGE,"E21");var subQ1=sQuery(id+"F0.wireOp",EDGE,"E3");var subQ2=makeQuery(id+"F0.imprint","INTERSECT",VERTEX,{"derivedFrom":[subQ1,subQ0]});Q71=makeQuery(id+"F0.imprint","IMPRINT",FACE,{"disambiguationData":[TD([[makeQuery(id+"F0.imprint","IMPRINT",EDGE,{"disambiguationData":[TD([[subQ2,-1.0]])],"derivedFrom":subQ1}),1.0]])]});}
            extrude(context, id + "F1", {"entities" : qUnion([Q0, Q1, Q2, Q3, Q4, Q5, Q6, Q7, Q8, Q9, Q10, Q11, Q12, Q13, Q14, Q15, Q16, Q17, Q18, Q19, Q20, Q21, Q22, Q23, Q24, Q25, Q26, Q27, Q28, Q29, Q30, Q31, Q32, Q33, Q34, Q35, Q36, Q37, Q38, Q39, Q40, Q41, Q42, Q43, Q44, Q45, Q46, Q47, Q48, Q49, Q50, Q51, Q52, Q53, Q54, Q55, Q56, Q57, Q58, Q59, Q60, Q61, Q62, Q63, Q64, Q65, Q66, Q67, Q68, Q69, Q70, Q71]), "depth" : 4.83 * mm, "offsetDistance" : 25.4 * mm});
        }
    });
